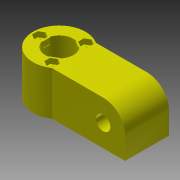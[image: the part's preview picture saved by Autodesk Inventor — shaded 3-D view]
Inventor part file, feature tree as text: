
AUTODESK INVENTOR PART (.ipt)
format: ipt  version: 2013 (Build 170138000, 138)  size: 168,448 bytes
history: native  units: mm
features: extrude x7, sketch x7, pattern_circular x1
ambient origin geometry x8: Origin, YZ Plane, XZ Plane, XY Plane, X Axis, Y Axis, Z Axis, Center Point
bodies: Solid1 (feature_tree)
feature tree (15):
  extrude  "Extrusion1"  Depth=25.0mm
  extrude  "Extrusion2"  Depth=25.0mm TaperAngle=0.0deg
  extrude  "Extrusion3"  Depth=8.2mm
  extrude  "Extrusion10"  Depth=13.2mm
  extrude  "Extrusion11"  Depth=38.1mm
  extrude  "Extrusion12"  Depth=14.2875mm
  extrude  "Extrusion13"  Depth=10.0mm TaperAngle=0.0deg
  pattern_circular  "Circular Pattern3"  [2 undecoded]
  sketch  "Sketch1"  dims[d0=19.25mm d2=25.0mm]
  sketch  "Sketch2"  dims[d4=37.5mm d5=25.0mm d6=0.0mm]
  sketch  "Sketch3"  dims[d7=25.0mm d8=0.0mm d9=8.2mm]
  sketch  "Sketch10"  dims[d11=25.0mm d12=0.0mm d47=13.2mm]
  sketch  "Sketch11"  dims[d48=8.0mm d49=0.0mm d50=38.1mm]
  sketch  "Sketch12"  dims[d53=10.0mm d54=0.0mm d55=14.2875mm]
  sketch  "Sketch13"  dims[d56=3.2mm d57=10.0mm d58=0.0mm d59=5.65mm d60=3.0mm d61=0.0mm d62=30.0mm d63=360.0deg]
note: 2 required parameter values undecoded (feature->parameter linkage not recoverable at this tier; creation-order binding heuristic only, values carry confidence <= 0.55)
